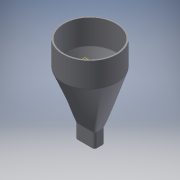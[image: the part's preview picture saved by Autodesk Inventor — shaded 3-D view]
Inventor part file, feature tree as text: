
AUTODESK INVENTOR PART (.ipt)
format: ipt  version: 2016 (Build 200138000, 138)  size: 1,050,624 bytes
history: native  units: mm
features: fillet x16, sketch x4, extrude x2, loft x2, other x2, plane x1
ambient origin geometry x8: Origin, YZ Plane, XZ Plane, XY Plane, X Axis, Y Axis, Z Axis, Center Point
bodies: Solid1 (feature_tree)
feature tree (27):
  extrude  "Extrusion1"  Depth=21.0mm
  plane  "Work Plane1"
  loft  "Loft2"
  loft  "Loft3"
  fillet  "Fillet10"  [1 undecoded]
  fillet  "Fillet11"  [1 undecoded]
  fillet  "Fillet12"  Radius=104.0mm
  fillet  "Fillet13"  [1 undecoded]
  fillet  "Fillet17"  [1 undecoded]
  extrude  "Extrusion3"  Depth=5.0mm
  fillet  "Fillet18"  Radius=12.0mm
  fillet  "Fillet19"  Radius=3.69mm
  fillet  "Fillet1"  Radius=11.2mm
  fillet  "Fillet2"  Radius=23.4mm
  fillet  "Fillet4"  Radius=2.0mm
  fillet  "Fillet15"  Radius=1.0mm
  fillet  "Fillet5"  Radius=10.0mm
  fillet  "Fillet6"  Radius=20.0mm
  fillet  "Fillet7"  Radius=5.0mm
  fillet  "Fillet8"  Radius=5.0mm
  fillet  "Fillet3"  Radius=2.0mm
  sketch  "Sketch1"  dims[d0=40.0mm d1=21.0mm]
  sketch  "Sketch2"  dims[d2=1.5mm d3=30.0mm d4=0.0mm]
  other  "Edges6"
  sketch  "Sketch3"  dims[d5=100.0mm d6=110.0mm d26=0.0mm d27=90.0deg d28=0.0mm d29=90.0deg d30=104.0mm d31=0.0mm d32=90.0deg d33=0.0mm d34=90.0deg]
  other  "Edges7"
  sketch  "Sketch4"  dims[d35=10.0mm d36=5.0mm d37=12.0mm d38=3.69mm d39=11.2mm d40=23.4mm d41=2.0mm d42=1.0mm d44=10.0mm d45=20.0mm d46=5.0mm d47=5.0mm d49=2.0mm d51=2.0mm d52=50.0mm d53=0.0mm d54=5.0mm d55=5.0mm]
note: 4 required parameter values undecoded (feature->parameter linkage not recoverable at this tier; creation-order binding heuristic only, values carry confidence <= 0.55)
